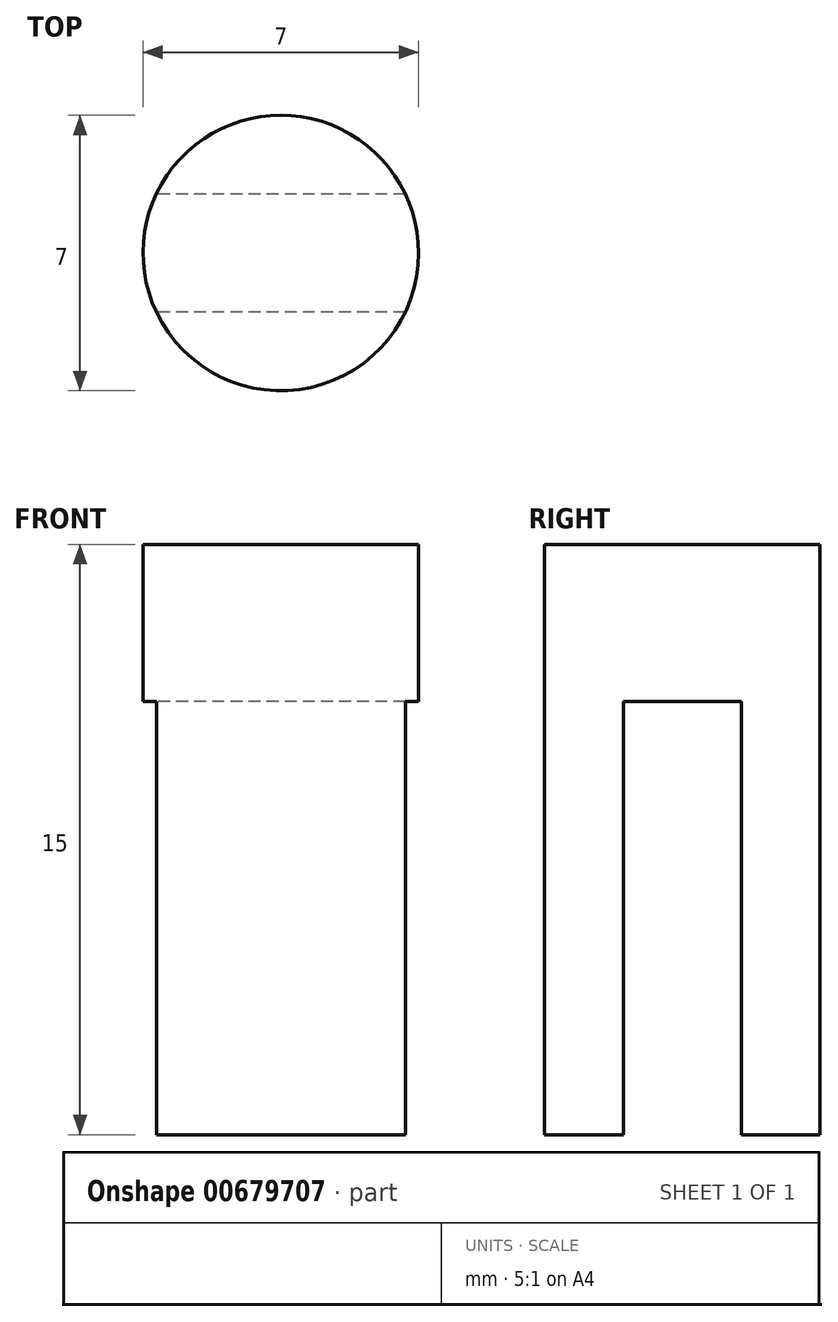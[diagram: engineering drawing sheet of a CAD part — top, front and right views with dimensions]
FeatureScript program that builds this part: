
annotation { "Feature Type Name" : "Feature", "Feature Type Description" : "" }
export const myFeature = defineFeature(function(context is Context, id is Id, definition is map)
    precondition{}
    {
        {
            var Q0;
            Q0=qCreatedBy(makeId("Top.planeOp"),FACE);
            var sketch = newSketch(context, id + "F0", { "sketchPlane" : qUnion([Q0])});
            skCircle(sketch, "E0", {"center": v(0, 0) * mm, "radius": 3.5 * mm});
            skSolve(sketch);
        }
        {
            var Q0;
            Q0=makeQuery(id+"F0.imprint","IMPRINT",FACE,{"disambiguationData":[TD([[makeQuery(id+"F0.imprint","IMPRINT",EDGE,{"derivedFrom":sQuery(id+"F0.wireOp",EDGE,"E0")}),1.0]])]});
            extrude(context, id + "F1", {"entities" : qUnion([Q0]), "depth" : 15 * mm, "offsetDistance" : 25.4 * mm});
        }
        {
            var Q0;
            Q0=qCreatedBy(makeId("Top.planeOp"),FACE);
            var sketch = newSketch(context, id + "F2", { "sketchPlane" : qUnion([Q0])});
            skLineSegment(sketch, "E1.bottom", {"start": v(6.37, -1.5) * mm, "end": v(-6.37, -1.5) * mm});
            skLineSegment(sketch, "E1.top", {"start": v(6.37, 1.5) * mm, "end": v(-6.37, 1.5) * mm});
            skLineSegment(sketch, "E1.left", {"start": v(6.37, -1.5) * mm, "end": v(6.37, 1.5) * mm});
            skLineSegment(sketch, "E1.right", {"start": v(-6.37, -1.5) * mm, "end": v(-6.37, 1.5) * mm});
            skPoint(sketch, "E1.middle", {"position": v(0, 0) * mm});
            skSolve(sketch);
        }
        {
            var Q0;
            Q0=makeQuery(id+"F2.imprint","IMPRINT",FACE,{"disambiguationData":[TD([[makeQuery(id+"F2.imprint","IMPRINT",EDGE,{"derivedFrom":sQuery(id+"F2.wireOp",EDGE,"E1.bottom")}),-1.0]])]});
            extrude(context, id + "F3", {"entities" : qUnion([Q0]), "operationType" : NewBodyOperationType.REMOVE, "depth" : 11 * mm, "offsetDistance" : 25.4 * mm});
        }
    });
